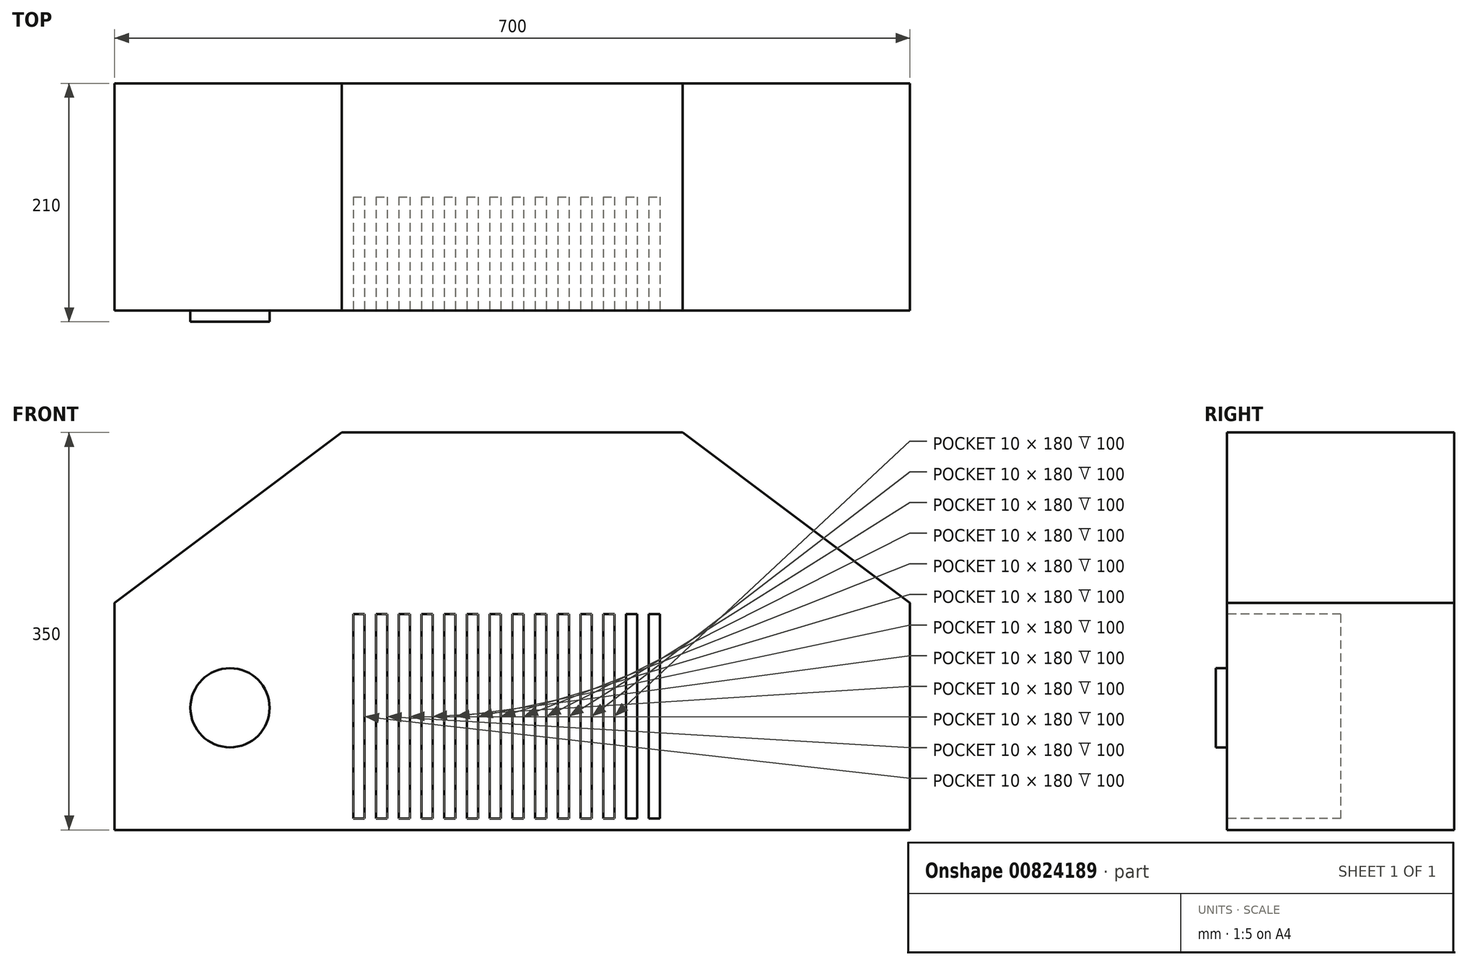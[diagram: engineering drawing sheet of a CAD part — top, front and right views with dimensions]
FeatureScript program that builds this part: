
annotation { "Feature Type Name" : "Feature", "Feature Type Description" : "" }
export const myFeature = defineFeature(function(context is Context, id is Id, definition is map)
    precondition{}
    {
        {
            var Q0;
            Q0=qCreatedBy(makeId("Front.planeOp"),FACE);
            var sketch = newSketch(context, id + "F0", { "sketchPlane" : qUnion([Q0])});
            skLineSegment(sketch, "E0.bottom", {"start": v(-237.63, 190.98) * mm, "end": v(462.37, 190.98) * mm});
            skLineSegment(sketch, "E0.top", {"start": v(-237.63, -9.02) * mm, "end": v(462.37, -9.02) * mm});
            skLineSegment(sketch, "E0.left", {"start": v(-237.63, 190.98) * mm, "end": v(-237.63, -9.02) * mm});
            skLineSegment(sketch, "E0.right", {"start": v(462.37, 190.98) * mm, "end": v(462.37, -9.02) * mm});
            skLineSegment(sketch, "E1", {"start": v(-37.63, -9.02) * mm, "end": v(-37.63, 190.98) * mm});
            skLineSegment(sketch, "E2", {"start": v(262.37, -9.02) * mm, "end": v(262.37, 190.98) * mm});
            skPoint(sketch, "E3.end.orphan", {"position": v(-37.63, -6.88) * mm});
            skPoint(sketch, "E4.end.orphan", {"position": v(262.37, 2.62) * mm});
            skLineSegment(sketch, "E5", {"start": v(-37.63, 190.98) * mm, "end": v(-37.63, 340.98) * mm});
            skLineSegment(sketch, "E6", {"start": v(-237.63, 190.98) * mm, "end": v(-37.63, 340.98) * mm});
            skLineSegment(sketch, "E7", {"start": v(262.37, 190.98) * mm, "end": v(262.37, 340.98) * mm});
            skPoint(sketch, "E8.orphan", {"position": v(262.37, 522.65) * mm});
            skLineSegment(sketch, "E9", {"start": v(-37.63, 340.98) * mm, "end": v(262.37, 340.98) * mm});
            skPoint(sketch, "E10.orphan", {"position": v(262.37, 356.81) * mm});
            skLineSegment(sketch, "E11", {"start": v(462.37, 190.98) * mm, "end": v(262.37, 340.98) * mm});
            skSolve(sketch);
        }
        {
            var Q0;
            Q0 = qSketchRegion(id + "F0", true);
            extrude(context, id + "F1", {"entities" : qUnion([Q0]), "depth" : 200 * mm, "offsetDistance" : 25 * mm});
        }
        {
            var Q0;
            Q0=makeQuery(id+"F1.opExtrude","CAP_FACE",FACE,{"disambiguationData":[OSD([sQuery(id+"F0.wireOp",EDGE,"E0.top"),sQuery(id+"F0.wireOp",EDGE,"E0.left"),sQuery(id+"F0.wireOp",EDGE,"E0.right"),sQuery(id+"F0.wireOp",EDGE,"E6"),sQuery(id+"F0.wireOp",EDGE,"E9"),sQuery(id+"F0.wireOp",EDGE,"E11")])],"isStart":false});
            var sketch = newSketch(context, id + "F2", { "sketchPlane" : qUnion([Q0])});
            skLineSegment(sketch, "E12", {"start": v(-237.63, 190.98) * mm, "end": v(462.37, 190.98) * mm});
            skLineSegment(sketch, "E13", {"start": v(-37.63, 340.98) * mm, "end": v(-37.63, -9.02) * mm});
            skLineSegment(sketch, "E14", {"start": v(262.37, 340.98) * mm, "end": v(262.37, -9.02) * mm});
            skLineSegment(sketch, "E15", {"start": v(-27.63, 0.98) * mm, "end": v(252.37, 0.98) * mm});
            skLineSegment(sketch, "E16", {"start": v(-27.63, 0.98) * mm, "end": v(-27.63, 180.98) * mm});
            skLineSegment(sketch, "E17", {"start": v(252.37, 180.98) * mm, "end": v(252.37, 0) * mm});
            skLineSegment(sketch, "E18", {"start": v(-27.63, 180.98) * mm, "end": v(252.37, 180.98) * mm});
            skLineSegment(sketch, "E19", {"start": v(-17.63, 180.98) * mm, "end": v(-17.63, 0) * mm});
            skLineSegment(sketch, "E20", {"start": v(-7.63, 180.98) * mm, "end": v(-7.63, 0) * mm});
            skLineSegment(sketch, "E21", {"start": v(2.37, 180.98) * mm, "end": v(2.37, 0) * mm});
            skLineSegment(sketch, "E22", {"start": v(12.37, 180.98) * mm, "end": v(12.37, 0) * mm});
            skLineSegment(sketch, "E23", {"start": v(22.37, 180.98) * mm, "end": v(22.37, 0) * mm});
            skLineSegment(sketch, "E24", {"start": v(32.37, 180.98) * mm, "end": v(32.37, 0) * mm});
            skLineSegment(sketch, "E25", {"start": v(42.37, 180.98) * mm, "end": v(42.37, 0) * mm});
            skLineSegment(sketch, "E26", {"start": v(52.37, 180.98) * mm, "end": v(52.37, 0) * mm});
            skLineSegment(sketch, "E27", {"start": v(62.37, 180.98) * mm, "end": v(62.37, 0) * mm});
            skLineSegment(sketch, "E28", {"start": v(72.37, 180.98) * mm, "end": v(72.37, 0) * mm});
            skLineSegment(sketch, "E29", {"start": v(82.37, 180.98) * mm, "end": v(82.37, 0) * mm});
            skLineSegment(sketch, "E30", {"start": v(92.37, 180.98) * mm, "end": v(92.37, 0) * mm});
            skLineSegment(sketch, "E31", {"start": v(102.37, 180.98) * mm, "end": v(102.37, 0) * mm});
            skLineSegment(sketch, "E32", {"start": v(112.37, 180.98) * mm, "end": v(112.37, 0) * mm});
            skLineSegment(sketch, "E33", {"start": v(122.37, 180.98) * mm, "end": v(122.37, 0) * mm});
            skLineSegment(sketch, "E34", {"start": v(132.37, 180.98) * mm, "end": v(132.37, 0) * mm});
            skLineSegment(sketch, "E35", {"start": v(142.37, 180.98) * mm, "end": v(142.37, 0) * mm});
            skLineSegment(sketch, "E36", {"start": v(152.37, 180.98) * mm, "end": v(152.37, 0) * mm});
            skLineSegment(sketch, "E37", {"start": v(162.37, 180.98) * mm, "end": v(162.37, 0) * mm});
            skLineSegment(sketch, "E38", {"start": v(172.37, 180.98) * mm, "end": v(172.37, 0) * mm});
            skLineSegment(sketch, "E39", {"start": v(182.37, 180.98) * mm, "end": v(182.37, 0) * mm});
            skLineSegment(sketch, "E40", {"start": v(192.37, 180.98) * mm, "end": v(192.37, 0) * mm});
            skLineSegment(sketch, "E41", {"start": v(202.37, 180.98) * mm, "end": v(202.37, 0.98) * mm});
            skLineSegment(sketch, "E42", {"start": v(212.37, 180.98) * mm, "end": v(212.37, 0) * mm});
            skLineSegment(sketch, "E43", {"start": v(222.37, 180.98) * mm, "end": v(222.37, 0.98) * mm});
            skLineSegment(sketch, "E44", {"start": v(232.37, 180.98) * mm, "end": v(232.37, 0.98) * mm});
            skLineSegment(sketch, "E45", {"start": v(242.37, 180.98) * mm, "end": v(242.37, 0.98) * mm});
            skSolve(sketch);
        }
        {
            var Q0;
            {var subQ0=sQuery(id+"F2.wireOp",EDGE,"E16");Q0=makeQuery(id+"F2.imprint","IMPRINT",FACE,{"disambiguationData":[TD([[makeQuery(id+"F2.imprint","IMPRINT",EDGE,{"derivedFrom":subQ0}),-1.0]])]});}
            var Q1;
            {var subQ0=sQuery(id+"F2.wireOp",EDGE,"E20");var subQ1=sQuery(id+"F2.wireOp",EDGE,"E15");var subQ2=makeQuery(id+"F2.imprint","INTERSECT",VERTEX,{"derivedFrom":[subQ1,subQ0]});Q1=makeQuery(id+"F2.imprint","IMPRINT",FACE,{"disambiguationData":[TD([[makeQuery(id+"F2.imprint","IMPRINT",EDGE,{"disambiguationData":[TD([[subQ2,-1.0]])],"derivedFrom":subQ1}),1.0]])]});}
            var Q2;
            {var subQ0=sQuery(id+"F2.wireOp",EDGE,"E22");var subQ1=sQuery(id+"F2.wireOp",EDGE,"E15");var subQ2=makeQuery(id+"F2.imprint","INTERSECT",VERTEX,{"derivedFrom":[subQ1,subQ0]});Q2=makeQuery(id+"F2.imprint","IMPRINT",FACE,{"disambiguationData":[TD([[makeQuery(id+"F2.imprint","IMPRINT",EDGE,{"disambiguationData":[TD([[subQ2,-1.0]])],"derivedFrom":subQ1}),1.0]])]});}
            var Q3;
            {var subQ0=sQuery(id+"F2.wireOp",EDGE,"E24");var subQ1=sQuery(id+"F2.wireOp",EDGE,"E15");var subQ2=makeQuery(id+"F2.imprint","INTERSECT",VERTEX,{"derivedFrom":[subQ1,subQ0]});Q3=makeQuery(id+"F2.imprint","IMPRINT",FACE,{"disambiguationData":[TD([[makeQuery(id+"F2.imprint","IMPRINT",EDGE,{"disambiguationData":[TD([[subQ2,-1.0]])],"derivedFrom":subQ1}),1.0]])]});}
            var Q4;
            {var subQ0=sQuery(id+"F2.wireOp",EDGE,"E26");var subQ1=sQuery(id+"F2.wireOp",EDGE,"E15");var subQ2=makeQuery(id+"F2.imprint","INTERSECT",VERTEX,{"derivedFrom":[subQ1,subQ0]});Q4=makeQuery(id+"F2.imprint","IMPRINT",FACE,{"disambiguationData":[TD([[makeQuery(id+"F2.imprint","IMPRINT",EDGE,{"disambiguationData":[TD([[subQ2,-1.0]])],"derivedFrom":subQ1}),1.0]])]});}
            var Q5;
            {var subQ0=sQuery(id+"F2.wireOp",EDGE,"E28");var subQ1=sQuery(id+"F2.wireOp",EDGE,"E15");var subQ2=makeQuery(id+"F2.imprint","INTERSECT",VERTEX,{"derivedFrom":[subQ1,subQ0]});Q5=makeQuery(id+"F2.imprint","IMPRINT",FACE,{"disambiguationData":[TD([[makeQuery(id+"F2.imprint","IMPRINT",EDGE,{"disambiguationData":[TD([[subQ2,-1.0]])],"derivedFrom":subQ1}),1.0]])]});}
            var Q6;
            {var subQ0=sQuery(id+"F2.wireOp",EDGE,"E30");var subQ1=sQuery(id+"F2.wireOp",EDGE,"E15");var subQ2=makeQuery(id+"F2.imprint","INTERSECT",VERTEX,{"derivedFrom":[subQ1,subQ0]});Q6=makeQuery(id+"F2.imprint","IMPRINT",FACE,{"disambiguationData":[TD([[makeQuery(id+"F2.imprint","IMPRINT",EDGE,{"disambiguationData":[TD([[subQ2,-1.0]])],"derivedFrom":subQ1}),1.0]])]});}
            var Q7;
            {var subQ0=sQuery(id+"F2.wireOp",EDGE,"E32");var subQ1=sQuery(id+"F2.wireOp",EDGE,"E15");var subQ2=makeQuery(id+"F2.imprint","INTERSECT",VERTEX,{"derivedFrom":[subQ1,subQ0]});Q7=makeQuery(id+"F2.imprint","IMPRINT",FACE,{"disambiguationData":[TD([[makeQuery(id+"F2.imprint","IMPRINT",EDGE,{"disambiguationData":[TD([[subQ2,-1.0]])],"derivedFrom":subQ1}),1.0]])]});}
            var Q8;
            {var subQ0=sQuery(id+"F2.wireOp",EDGE,"E34");var subQ1=sQuery(id+"F2.wireOp",EDGE,"E15");var subQ2=makeQuery(id+"F2.imprint","INTERSECT",VERTEX,{"derivedFrom":[subQ1,subQ0]});Q8=makeQuery(id+"F2.imprint","IMPRINT",FACE,{"disambiguationData":[TD([[makeQuery(id+"F2.imprint","IMPRINT",EDGE,{"disambiguationData":[TD([[subQ2,-1.0]])],"derivedFrom":subQ1}),1.0]])]});}
            var Q9;
            {var subQ0=sQuery(id+"F2.wireOp",EDGE,"E36");var subQ1=sQuery(id+"F2.wireOp",EDGE,"E15");var subQ2=makeQuery(id+"F2.imprint","INTERSECT",VERTEX,{"derivedFrom":[subQ1,subQ0]});Q9=makeQuery(id+"F2.imprint","IMPRINT",FACE,{"disambiguationData":[TD([[makeQuery(id+"F2.imprint","IMPRINT",EDGE,{"disambiguationData":[TD([[subQ2,-1.0]])],"derivedFrom":subQ1}),1.0]])]});}
            var Q10;
            {var subQ0=sQuery(id+"F2.wireOp",EDGE,"E38");var subQ1=sQuery(id+"F2.wireOp",EDGE,"E15");var subQ2=makeQuery(id+"F2.imprint","INTERSECT",VERTEX,{"derivedFrom":[subQ1,subQ0]});Q10=makeQuery(id+"F2.imprint","IMPRINT",FACE,{"disambiguationData":[TD([[makeQuery(id+"F2.imprint","IMPRINT",EDGE,{"disambiguationData":[TD([[subQ2,-1.0]])],"derivedFrom":subQ1}),1.0]])]});}
            var Q11;
            {var subQ0=sQuery(id+"F2.wireOp",EDGE,"E41");Q11=makeQuery(id+"F2.imprint","IMPRINT",FACE,{"disambiguationData":[TD([[makeQuery(id+"F2.imprint","IMPRINT",EDGE,{"derivedFrom":subQ0}),-1.0]])]});}
            var Q12;
            {var subQ0=sQuery(id+"F2.wireOp",EDGE,"E43");Q12=makeQuery(id+"F2.imprint","IMPRINT",FACE,{"disambiguationData":[TD([[makeQuery(id+"F2.imprint","IMPRINT",EDGE,{"derivedFrom":subQ0}),-1.0]])]});}
            var Q13;
            {var subQ0=sQuery(id+"F2.wireOp",EDGE,"E44");Q13=makeQuery(id+"F2.imprint","IMPRINT",FACE,{"disambiguationData":[TD([[makeQuery(id+"F2.imprint","IMPRINT",EDGE,{"derivedFrom":subQ0}),1.0]])]});}
            extrude(context, id + "F3", {"entities" : qUnion([Q0, Q1, Q2, Q3, Q4, Q5, Q6, Q7, Q8, Q9, Q10, Q11, Q12, Q13]), "operationType" : NewBodyOperationType.REMOVE, "oppositeDirection" : true, "depth" : 100 * mm, "offsetDistance" : 25 * mm});
        }
        {
            var Q0;
            Q0=makeQuery(id+"F1.opExtrude","CAP_FACE",FACE,{"disambiguationData":[OSD([sQuery(id+"F0.wireOp",EDGE,"E0.top"),sQuery(id+"F0.wireOp",EDGE,"E0.left"),sQuery(id+"F0.wireOp",EDGE,"E0.right"),sQuery(id+"F0.wireOp",EDGE,"E6"),sQuery(id+"F0.wireOp",EDGE,"E9"),sQuery(id+"F0.wireOp",EDGE,"E11")])],"isStart":false});
            var sketch = newSketch(context, id + "F4", { "sketchPlane" : qUnion([Q0])});
            skCircle(sketch, "E46", {"center": v(-136.07, 98.52) * mm, "radius": 34.87 * mm});
            skSolve(sketch);
        }
        {
            var Q0;
            Q0=makeQuery(id+"F4.imprint","IMPRINT",FACE,{"disambiguationData":[TD([[makeQuery(id+"F4.imprint","IMPRINT",EDGE,{"derivedFrom":sQuery(id+"F4.wireOp",EDGE,"E46")}),1.0]])]});
            extrude(context, id + "F5", {"entities" : qUnion([Q0]), "operationType" : NewBodyOperationType.ADD, "depth" : 10 * mm, "offsetDistance" : 25 * mm});
        }
    });
